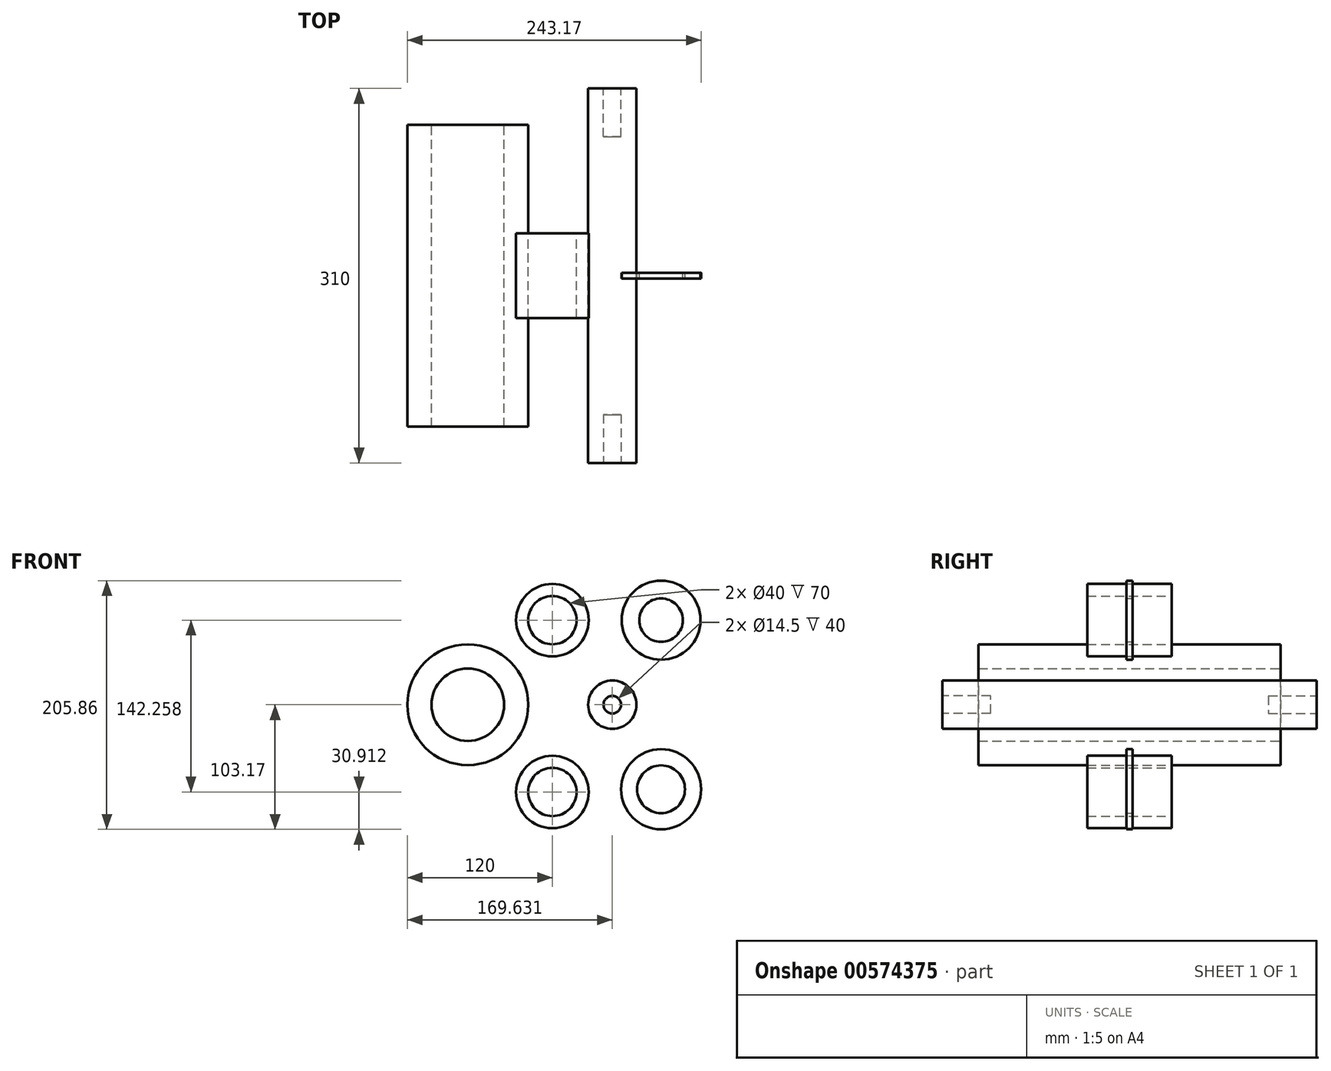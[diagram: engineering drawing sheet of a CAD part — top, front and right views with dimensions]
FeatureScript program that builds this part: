
annotation { "Feature Type Name" : "Feature", "Feature Type Description" : "" }
export const myFeature = defineFeature(function(context is Context, id is Id, definition is map)
    precondition{}
    {
        {
            var Q0;
            Q0=qCreatedBy(makeId("Front.planeOp"),FACE);
            var sketch = newSketch(context, id + "F0", { "sketchPlane" : qUnion([Q0])});
            skCircle(sketch, "E0", {"center": v(-70, 0) * mm, "radius": 50 * mm});
            skCircle(sketch, "E1", {"center": v(-70, 0) * mm, "radius": 30 * mm});
            skSolve(sketch);
        }
        {
            var Q0;
            Q0=makeQuery(id+"F0.imprint","IMPRINT",FACE,{"disambiguationData":[TD([[makeQuery(id+"F0.imprint","IMPRINT",EDGE,{"derivedFrom":sQuery(id+"F0.wireOp",EDGE,"E0")}),1.0]])]});
            extrude(context, id + "F1", {"entities" : qUnion([Q0]), "endBound" : BoundingType.SYMMETRIC, "depth" : 250 * mm, "offsetDistance" : 25 * mm});
        }
        {
            var Q0;
            Q0=qCreatedBy(makeId("Front.planeOp"),FACE);
            var sketch = newSketch(context, id + "F2", { "sketchPlane" : qUnion([Q0])});
            skCircle(sketch, "E2", {"center": v(0, 70) * mm, "radius": 20 * mm});
            skCircle(sketch, "E3", {"center": v(0, 70) * mm, "radius": 30 * mm});
            skCircle(sketch, "E4", {"center": v(0, -72.26) * mm, "radius": 30 * mm});
            skCircle(sketch, "E5", {"center": v(0, -72.26) * mm, "radius": 20 * mm});
            skSolve(sketch);
        }
        {
            var Q0;
            Q0=makeQuery(id+"F2.imprint","IMPRINT",FACE,{"disambiguationData":[TD([[makeQuery(id+"F2.imprint","IMPRINT",EDGE,{"derivedFrom":sQuery(id+"F2.wireOp",EDGE,"E2")}),-1.0]])]});
            var Q1;
            Q1=makeQuery(id+"F2.imprint","IMPRINT",FACE,{"disambiguationData":[TD([[makeQuery(id+"F2.imprint","IMPRINT",EDGE,{"derivedFrom":sQuery(id+"F2.wireOp",EDGE,"E4")}),1.0]])]});
            extrude(context, id + "F3", {"entities" : qUnion([Q0, Q1]), "endBound" : BoundingType.SYMMETRIC, "depth" : 70 * mm, "offsetDistance" : 25 * mm});
        }
        {
            var Q0;
            Q0=qCreatedBy(makeId("Front.planeOp"),FACE);
            var sketch = newSketch(context, id + "F4", { "sketchPlane" : qUnion([Q0])});
            skCircle(sketch, "E6", {"center": v(90, 70) * mm, "radius": 32.7 * mm});
            skCircle(sketch, "E7", {"center": v(90, -70) * mm, "radius": 33.17 * mm});
            skCircle(sketch, "E8", {"center": v(90, -70) * mm, "radius": 19.78 * mm});
            skCircle(sketch, "E9", {"center": v(90, 70) * mm, "radius": 18 * mm});
            skSolve(sketch);
        }
        {
            var Q0;
            Q0=makeQuery(id+"F4.imprint","IMPRINT",FACE,{"disambiguationData":[TD([[makeQuery(id+"F4.imprint","IMPRINT",EDGE,{"derivedFrom":sQuery(id+"F4.wireOp",EDGE,"E6")}),1.0]])]});
            var Q1;
            Q1=makeQuery(id+"F4.imprint","IMPRINT",FACE,{"disambiguationData":[TD([[makeQuery(id+"F4.imprint","IMPRINT",EDGE,{"derivedFrom":sQuery(id+"F4.wireOp",EDGE,"E7")}),1.0]])]});
            extrude(context, id + "F5", {"entities" : qUnion([Q0, Q1]), "endBound" : BoundingType.SYMMETRIC, "depth" : 5 * mm, "offsetDistance" : 25 * mm});
        }
        {
            var Q0;
            Q0=qCreatedBy(makeId("Front.planeOp"),FACE);
            var sketch = newSketch(context, id + "F6", { "sketchPlane" : qUnion([Q0])});
            skCircle(sketch, "E10", {"center": v(49.63, 0) * mm, "radius": 20 * mm});
            skSolve(sketch);
        }
        {
            var Q0;
            Q0 = qSketchRegion(id + "F6", true);
            extrude(context, id + "F7", {"entities" : qUnion([Q0]), "endBound" : BoundingType.SYMMETRIC, "depth" : 310 * mm, "offsetDistance" : 25 * mm});
        }
        {
            var Q0;
            Q0=makeQuery(id+"F7.opExtrude","CAP_FACE",FACE,{"disambiguationData":[OSD([sQuery(id+"F6.wireOp",EDGE,"E10")])],"isStart":false});
            var sketch = newSketch(context, id + "F8", { "sketchPlane" : qUnion([Q0])});
            skCircle(sketch, "E11.0.0", {"center": v(49.63, 0) * mm, "radius": 20 * mm});
            skCircle(sketch, "E12", {"center": v(49.63, 0) * mm, "radius": 7.25 * mm});
            skSolve(sketch);
        }
        {
            var Q0;
            Q0=makeQuery(id+"F8.imprint","IMPRINT",FACE,{"disambiguationData":[TD([[makeQuery(id+"F8.imprint","IMPRINT",EDGE,{"derivedFrom":sQuery(id+"F8.wireOp",EDGE,"E12")}),1.0]])]});
            extrude(context, id + "F9", {"entities" : qUnion([Q0]), "operationType" : NewBodyOperationType.REMOVE, "oppositeDirection" : true, "depth" : 40 * mm, "offsetDistance" : 25 * mm});
        }
        {
            var Q0;
            Q0=makeQuery(id+"F7.opExtrude","CAP_FACE",FACE,{"disambiguationData":[OSD([sQuery(id+"F6.wireOp",EDGE,"E10")])],"isStart":true});
            var sketch = newSketch(context, id + "F10", { "sketchPlane" : qUnion([Q0])});
            skCircle(sketch, "E13.0.0", {"center": v(-49.63, 0) * mm, "radius": 20 * mm});
            skCircle(sketch, "E14", {"center": v(-49.63, 0) * mm, "radius": 7.25 * mm});
            skSolve(sketch);
        }
        {
            var Q0;
            Q0=makeQuery(id+"F10.imprint","IMPRINT",FACE,{"disambiguationData":[TD([[makeQuery(id+"F10.imprint","IMPRINT",EDGE,{"derivedFrom":sQuery(id+"F10.wireOp",EDGE,"E14")}),1.0]])]});
            extrude(context, id + "F11", {"entities" : qUnion([Q0]), "operationType" : NewBodyOperationType.REMOVE, "depth" : -40 * mm, "offsetDistance" : 25 * mm});
        }
    });
